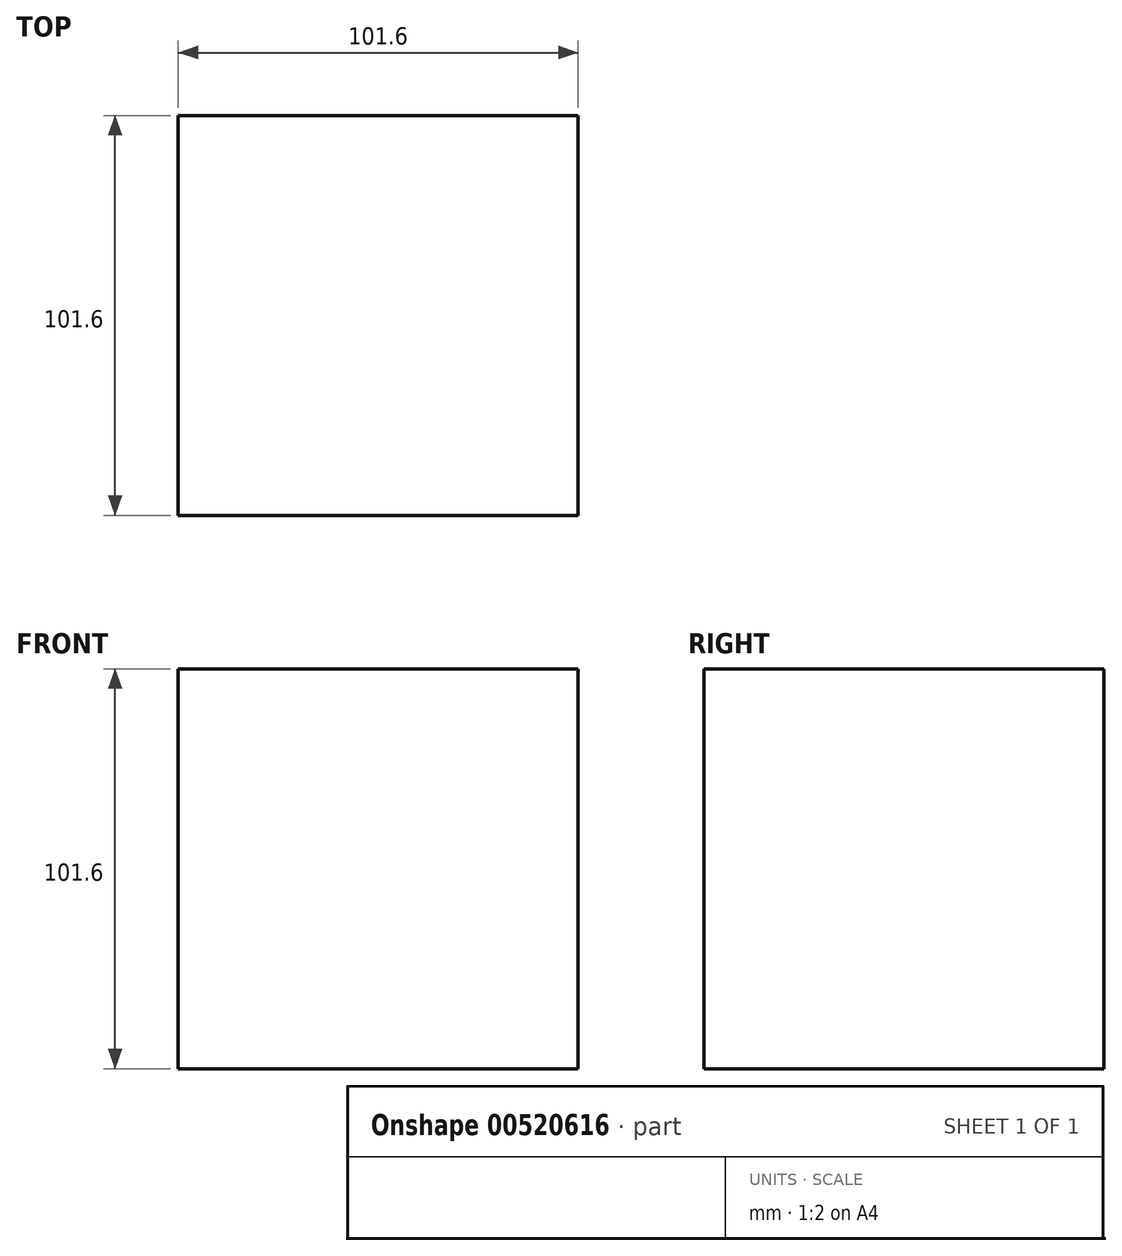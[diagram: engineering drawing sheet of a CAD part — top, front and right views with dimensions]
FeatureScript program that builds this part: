
annotation { "Feature Type Name" : "Feature", "Feature Type Description" : "" }
export const myFeature = defineFeature(function(context is Context, id is Id, definition is map)
    precondition{}
    {
        {
            var Q0;
            Q0=qCreatedBy(makeId("Front.planeOp"),FACE);
            var sketch = newSketch(context, id + "F0", { "sketchPlane" : qUnion([Q0])});
            skLineSegment(sketch, "E0", {"start": v(0, 0) * mm, "end": v(101.6, 0) * mm});
            skLineSegment(sketch, "E1", {"start": v(101.6, 0) * mm, "end": v(101.6, 101.6) * mm});
            skLineSegment(sketch, "E2", {"start": v(101.6, 101.6) * mm, "end": v(0, 101.6) * mm});
            skLineSegment(sketch, "E3", {"start": v(0, 101.6) * mm, "end": v(0, 0) * mm});
            skSolve(sketch);
        }
        {
            var Q0;
            Q0=makeQuery(id+"F0.imprint","IMPRINT",FACE,{"disambiguationData":[TD([[makeQuery(id+"F0.imprint","IMPRINT",EDGE,{"derivedFrom":sQuery(id+"F0.wireOp",EDGE,"E0")}),1.0]])]});
            extrude(context, id + "F1", {"entities" : qUnion([Q0]), "depth" : 101.6 * mm, "offsetDistance" : 25.4 * mm});
        }
    });
